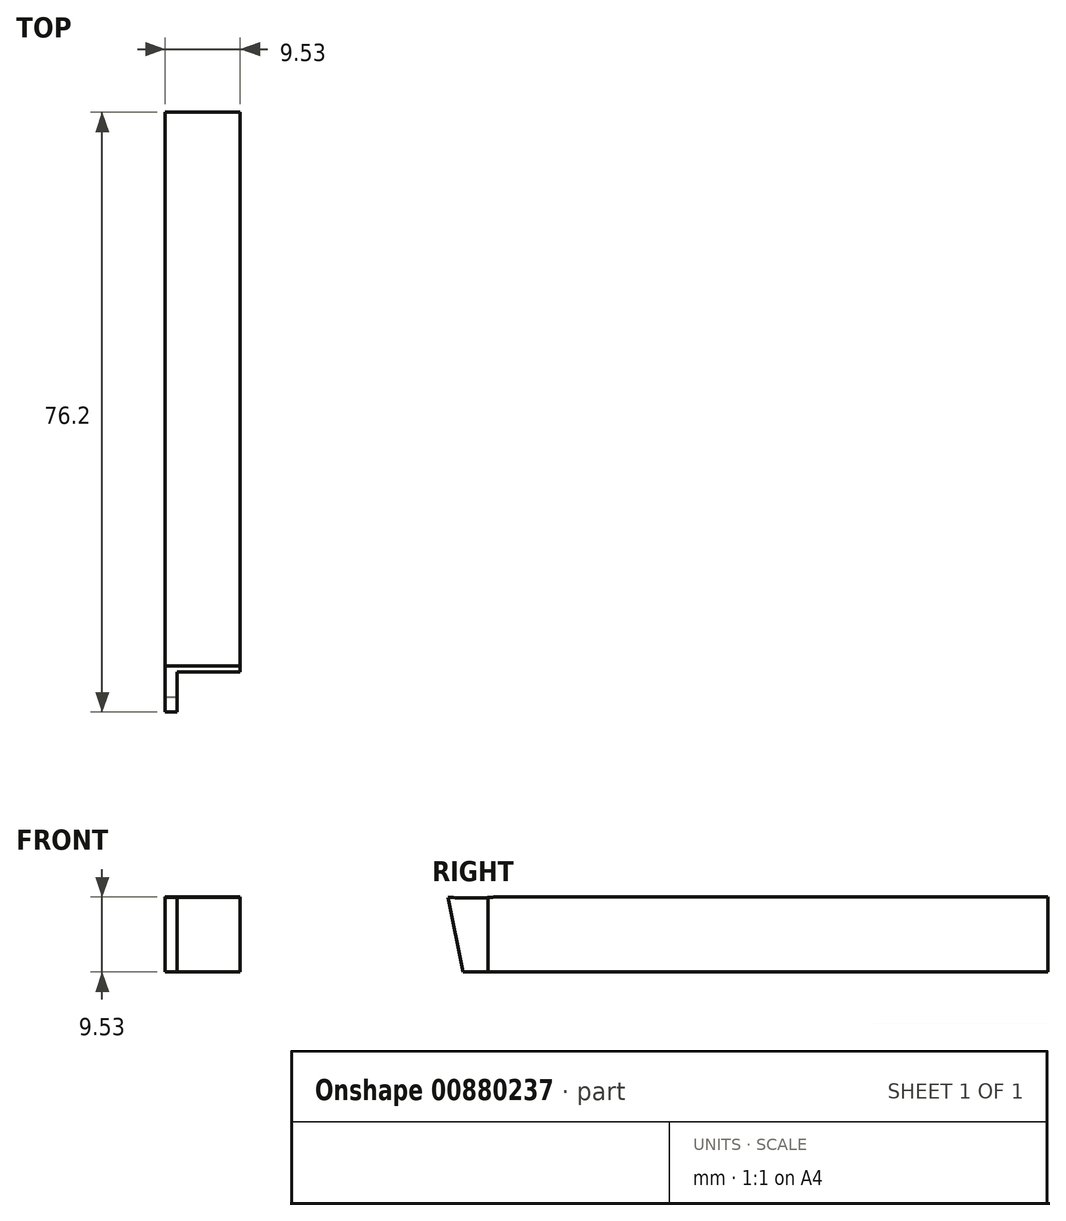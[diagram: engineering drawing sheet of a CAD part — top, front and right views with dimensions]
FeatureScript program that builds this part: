
annotation { "Feature Type Name" : "Feature", "Feature Type Description" : "" }
export const myFeature = defineFeature(function(context is Context, id is Id, definition is map)
    precondition{}
    {
        {
            var Q0;
            Q0=qCreatedBy(makeId("Top.planeOp"),FACE);
            var sketch = newSketch(context, id + "F0", { "sketchPlane" : qUnion([Q0])});
            skLineSegment(sketch, "E0.bottom", {"start": v(0, 0) * mm, "end": v(9.53, 0) * mm});
            skLineSegment(sketch, "E0.top", {"start": v(0, 76.2) * mm, "end": v(9.52, 76.2) * mm});
            skLineSegment(sketch, "E0.left", {"start": v(0, 0) * mm, "end": v(0, 76.2) * mm});
            skLineSegment(sketch, "E0.right", {"start": v(9.53, 0) * mm, "end": v(9.53, 76.2) * mm});
            skSolve(sketch);
        }
        {
            var Q0;
            Q0=qSketchRegion(id+"F0",true);
            extrude(context, id + "F1", {"entities" : qUnion([Q0]), "depth" : 9.52 * mm});
        }
        {
            var Q0;
            Q0=makeQuery(id+"F1.opExtrude","CAP_FACE",FACE,{"disambiguationData":[OSD([sQuery(id+"F0.wireOp",EDGE,"E0.bottom"),sQuery(id+"F0.wireOp",EDGE,"E0.top"),sQuery(id+"F0.wireOp",EDGE,"E0.left"),sQuery(id+"F0.wireOp",EDGE,"E0.right")])],"isStart":false});
            var sketch = newSketch(context, id + "F2", { "sketchPlane" : qUnion([Q0])});
            skLineSegment(sketch, "E1", {"start": v(1.52, -3.86) * mm, "end": v(1.52, 5.08) * mm});
            skLineSegment(sketch, "E2", {"start": v(1.52, 5.08) * mm, "end": v(13.94, 5.08) * mm});
            skLineSegment(sketch, "E3", {"start": v(13.94, 5.08) * mm, "end": v(13.94, -4.22) * mm});
            skLineSegment(sketch, "E4", {"start": v(13.94, -4.22) * mm, "end": v(1.52, -3.86) * mm});
            skSolve(sketch);
        }
        {
            var Q0;
            {var subQ0=sQuery(id+"F2.wireOp",EDGE,"E3");Q0=makeQuery(id+"F2.imprint","IMPRINT",FACE,{"disambiguationData":[TD([[makeQuery(id+"F2.imprint","IMPRINT",EDGE,{"derivedFrom":subQ0}),-1.0]])]});}
            var Q1;
            {var subQ0=sQuery(id+"F2.wireOp",EDGE,"E2");var subQ1=sQuery(id+"F2.wireOp",EDGE,"E1");var subQ2=makeQuery(id+"F2.imprint","INTERSECT",VERTEX,{"derivedFrom":[subQ1,subQ0]});Q1=makeQuery(id+"F2.imprint","IMPRINT",FACE,{"disambiguationData":[TD([[makeQuery(id+"F2.imprint","IMPRINT",EDGE,{"disambiguationData":[TD([[subQ2,1.0]])],"derivedFrom":subQ1}),-1.0]])]});}
            extrude(context, id + "F3", {"entities" : qUnion([Q0, Q1]), "operationType" : NewBodyOperationType.REMOVE, "oppositeDirection" : true, "depth" : 25.4 * mm});
        }
        {
            var Q0;
            Q0=makeQuery(id+"F1.opExtrude","SWEPT_FACE",FACE,{"disambiguationData":[OSD([sQuery(id+"F0.wireOp",EDGE,"E0.right")])]});
            var sketch = newSketch(context, id + "F4", { "sketchPlane" : qUnion([Q0])});
            skCircle(sketch, "E5", {"center": v(2.74, 48.62) * mm, "radius": 39.22 * mm});
            skSolve(sketch);
        }
        {
            var Q0;
            Q0=qSketchRegion(id+"F4",true);
            extrude(context, id + "F5", {"entities" : qUnion([Q0]), "operationType" : NewBodyOperationType.REMOVE, "oppositeDirection" : true, "depth" : 25.4 * mm});
        }
        {
            var Q0;
            Q0=makeQuery(id+"F1.opExtrude","SWEPT_FACE",FACE,{"disambiguationData":[OSD([sQuery(id+"F0.wireOp",EDGE,"E0.right")])]});
            var sketch = newSketch(context, id + "F6", { "sketchPlane" : qUnion([Q0])});
            skLineSegment(sketch, "E6", {"start": v(0, 9.5) * mm, "end": v(2.3, -2.03) * mm});
            skLineSegment(sketch, "E7.0", {"start": v(0, 9.5) * mm, "end": v(0, 0) * mm});
            skLineSegment(sketch, "E8", {"start": v(0, 0) * mm, "end": v(2.3, -2.03) * mm});
            skSolve(sketch);
        }
        {
            var Q0;
            Q0=qSketchRegion(id+"F6",true);
            extrude(context, id + "F7", {"entities" : qUnion([Q0]), "operationType" : NewBodyOperationType.REMOVE, "oppositeDirection" : true, "depth" : 25.4 * mm});
        }
    });
